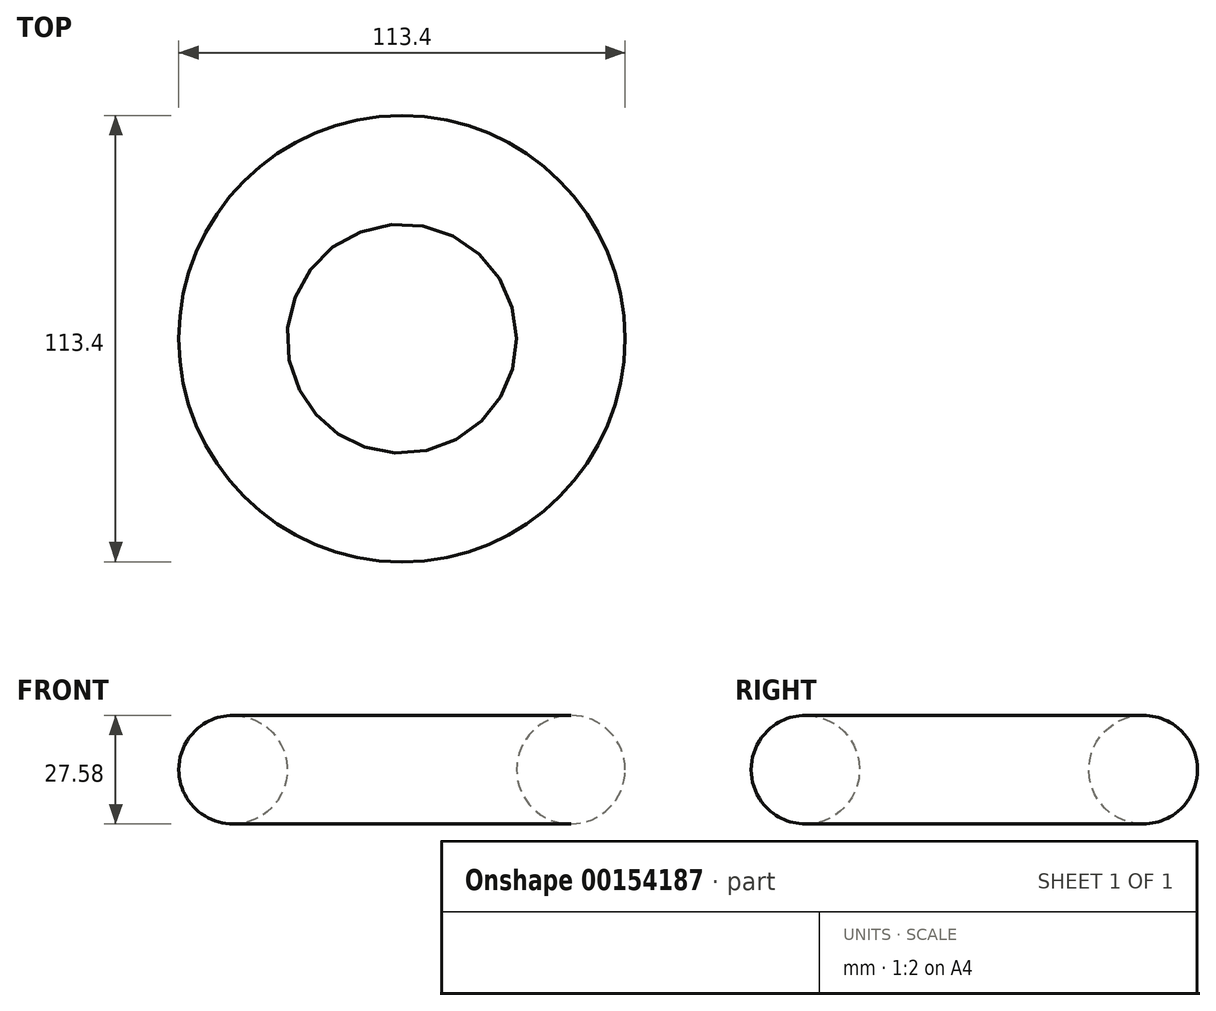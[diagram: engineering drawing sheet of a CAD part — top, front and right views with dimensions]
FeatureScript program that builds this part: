
annotation { "Feature Type Name" : "Feature", "Feature Type Description" : "" }
export const myFeature = defineFeature(function(context is Context, id is Id, definition is map)
    precondition{}
    {
        {
            var Q0;
            Q0=qCreatedBy(makeId("Front.planeOp"),FACE);
            var sketch = newSketch(context, id + "F0", { "sketchPlane" : qUnion([Q0])});
            skCircle(sketch, "E0", {"center": v(-42.91, 0) * mm, "radius": 13.79 * mm});
            skLineSegment(sketch, "E1", {"start": v(0, 0) * mm, "end": v(0, 103.92) * mm});
            skSolve(sketch);
        }
        {
            var Q0;
            Q0=sQuery(id+"F0.wireOp",EDGE,"E0");
            var Q1;
            Q1=sQuery(id+"F0.wireOp",EDGE,"E1");
            revolve(context, id + "F1", {"bodyType" : ToolBodyType.SURFACE, "surfaceEntities" : qUnion([Q0]), "axis" : qUnion([Q1]), "revolveType" : RevolveType.FULL});
        }
    });
